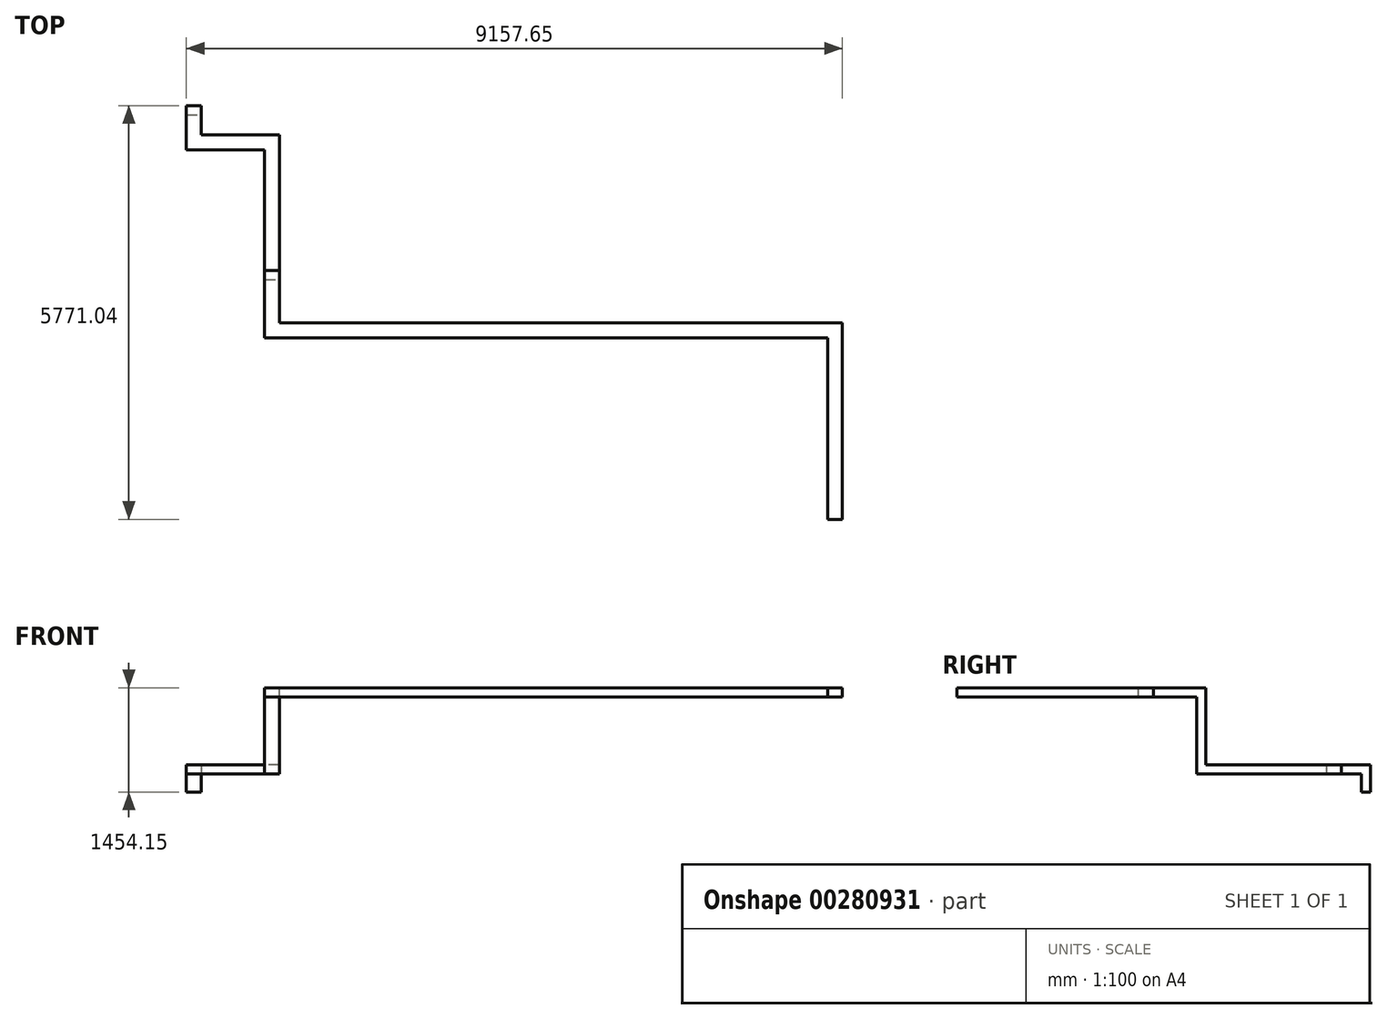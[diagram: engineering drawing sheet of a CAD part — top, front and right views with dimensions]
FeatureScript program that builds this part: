
annotation { "Feature Type Name" : "Feature", "Feature Type Description" : "" }
export const myFeature = defineFeature(function(context is Context, id is Id, definition is map)
    precondition{}
    {
        {
            var Q0;
            Q0=qCreatedBy(makeId("Top.planeOp"),FACE);
            var sketch = newSketch(context, id + "F0", { "sketchPlane" : qUnion([Q0])});
            skLineSegment(sketch, "E0.bottom", {"start": v(0, 0) * mm, "end": v(208.28, 0) * mm});
            skLineSegment(sketch, "E0.top", {"start": v(0, 127) * mm, "end": v(208.28, 127) * mm});
            skLineSegment(sketch, "E0.left", {"start": v(0, 0) * mm, "end": v(0, 127) * mm});
            skLineSegment(sketch, "E0.right", {"start": v(208.28, 0) * mm, "end": v(208.28, 127) * mm});
            skSolve(sketch);
        }
        {
            var Q0;
            Q0=makeQuery(id+"F0.imprint","IMPRINT",FACE,{"disambiguationData":[TD([[makeQuery(id+"F0.imprint","IMPRINT",EDGE,{"derivedFrom":sQuery(id+"F0.wireOp",EDGE,"E0.bottom")}),1.0]])]});
            extrude(context, id + "F1", {"entities" : qUnion([Q0]), "depth" : 381 * mm});
        }
        {
            var Q0;
            Q0=makeQuery(id+"F1.opExtrude","SWEPT_FACE",FACE,{"disambiguationData":[OSD([sQuery(id+"F0.wireOp",EDGE,"E0.bottom")])]});
            var sketch = newSketch(context, id + "F2", { "sketchPlane" : qUnion([Q0])});
            skLineSegment(sketch, "E1.bottom", {"start": v(0, 381) * mm, "end": v(208.28, 381) * mm});
            skLineSegment(sketch, "E1.top", {"start": v(0, 254) * mm, "end": v(208.28, 254) * mm});
            skLineSegment(sketch, "E1.left", {"start": v(0, 381) * mm, "end": v(0, 254) * mm});
            skLineSegment(sketch, "E1.right", {"start": v(208.28, 381) * mm, "end": v(208.28, 254) * mm});
            skSolve(sketch);
        }
        {
            var Q0;
            Q0=makeQuery(id+"F2.imprint","IMPRINT",FACE,{"disambiguationData":[TD([[makeQuery(id+"F2.imprint","IMPRINT",EDGE,{"derivedFrom":sQuery(id+"F2.wireOp",EDGE,"E1.bottom")}),-1.0]])]});
            extrude(context, id + "F3", {"entities" : qUnion([Q0]), "operationType" : NewBodyOperationType.ADD, "depth" : 1524 * mm});
        }
        {
            var Q0;
            Q0=makeQuery(id+"F3.opExtrude","CAP_FACE",FACE,{"disambiguationData":[OSD([sQuery(id+"F2.wireOp",EDGE,"E1.bottom"),sQuery(id+"F2.wireOp",EDGE,"E1.top"),sQuery(id+"F2.wireOp",EDGE,"E1.left"),sQuery(id+"F2.wireOp",EDGE,"E1.right")])],"isStart":false});
            extrude(context, id + "F4", {"entities" : qUnion([Q0]), "operationType" : NewBodyOperationType.ADD, "depth" : 1612.9 * mm});
        }
        {
            var Q0;
            {var subQ0=sQuery(id+"F2.wireOp",EDGE,"E1.bottom");Q0=makeQuery(id+"F4.boolean.opBoolean","MERGE",FACE,{"derivedFrom":[makeQuery(id+"F3.boolean.opBoolean","MERGE",FACE,{"derivedFrom":[makeQuery(id+"F1.opExtrude","CAP_FACE",FACE,{"disambiguationData":[OSD([sQuery(id+"F0.wireOp",EDGE,"E0.bottom"),sQuery(id+"F0.wireOp",EDGE,"E0.top"),sQuery(id+"F0.wireOp",EDGE,"E0.left"),sQuery(id+"F0.wireOp",EDGE,"E0.right")])],"isStart":false}),makeQuery(id+"F3.opExtrude","SWEPT_FACE",FACE,{"disambiguationData":[OSD([subQ0])]})]}),makeQuery(id+"F4.opExtrude","SWEPT_FACE",FACE,{"disambiguationData":[OSD([subQ0])]})]});}
            var sketch = newSketch(context, id + "F5", { "sketchPlane" : qUnion([Q0])});
            skLineSegment(sketch, "E2.bottom", {"start": v(208.28, -3136.9) * mm, "end": v(0, -3136.9) * mm});
            skLineSegment(sketch, "E2.top", {"start": v(208.28, -3009.9) * mm, "end": v(0, -3009.9) * mm});
            skLineSegment(sketch, "E2.left", {"start": v(208.28, -3136.9) * mm, "end": v(208.28, -3009.9) * mm});
            skLineSegment(sketch, "E2.right", {"start": v(0, -3136.9) * mm, "end": v(0, -3009.9) * mm});
            skSolve(sketch);
        }
        {
            var Q0;
            Q0=makeQuery(id+"F5.imprint","IMPRINT",FACE,{"disambiguationData":[TD([[makeQuery(id+"F5.imprint","IMPRINT",EDGE,{"derivedFrom":sQuery(id+"F5.wireOp",EDGE,"E2.bottom")}),1.0]])]});
            extrude(context, id + "F6", {"entities" : qUnion([Q0]), "operationType" : NewBodyOperationType.ADD, "depth" : 863.6 * mm});
        }
        {
            var Q0;
            {var subQ0=sQuery(id+"F2.wireOp",EDGE,"E1.right");Q0=makeQuery(id+"F6.boolean.opBoolean","MERGE",FACE,{"derivedFrom":[makeQuery(id+"F4.boolean.opBoolean","MERGE",FACE,{"derivedFrom":[makeQuery(id+"F3.boolean.opBoolean","MERGE",FACE,{"derivedFrom":[makeQuery(id+"F1.opExtrude","SWEPT_FACE",FACE,{"disambiguationData":[OSD([sQuery(id+"F0.wireOp",EDGE,"E0.right")])]}),makeQuery(id+"F3.opExtrude","SWEPT_FACE",FACE,{"disambiguationData":[OSD([subQ0])]})]}),makeQuery(id+"F4.opExtrude","SWEPT_FACE",FACE,{"disambiguationData":[OSD([subQ0])]})]}),makeQuery(id+"F6.opExtrude","SWEPT_FACE",FACE,{"disambiguationData":[OSD([sQuery(id+"F5.wireOp",EDGE,"E2.left")])]})]});}
            var sketch = newSketch(context, id + "F7", { "sketchPlane" : qUnion([Q0])});
            skLineSegment(sketch, "E3.bottom", {"start": v(-3136.9, 1244.6) * mm, "end": v(-3009.9, 1244.6) * mm});
            skLineSegment(sketch, "E3.top", {"start": v(-3136.9, 1036.32) * mm, "end": v(-3009.9, 1036.32) * mm});
            skLineSegment(sketch, "E3.left", {"start": v(-3136.9, 1244.6) * mm, "end": v(-3136.9, 1036.32) * mm});
            skLineSegment(sketch, "E3.right", {"start": v(-3009.9, 1244.6) * mm, "end": v(-3009.9, 1036.32) * mm});
            skSolve(sketch);
        }
        {
            var Q0;
            Q0=makeQuery(id+"F7.imprint","IMPRINT",FACE,{"disambiguationData":[TD([[makeQuery(id+"F7.imprint","IMPRINT",EDGE,{"derivedFrom":sQuery(id+"F7.wireOp",EDGE,"E3.bottom")}),-1.0]])]});
            extrude(context, id + "F8", {"entities" : qUnion([Q0]), "operationType" : NewBodyOperationType.ADD, "depth" : 7112 * mm});
        }
        {
            var Q0;
            Q0=makeQuery(id+"F8.boolean.opBoolean","MERGE",FACE,{"derivedFrom":[makeQuery(id+"F6.opExtrude","SWEPT_FACE",FACE,{"disambiguationData":[OSD([sQuery(id+"F5.wireOp",EDGE,"E2.top")])]}),makeQuery(id+"F8.opExtrude","SWEPT_FACE",FACE,{"disambiguationData":[OSD([sQuery(id+"F7.wireOp",EDGE,"E3.right")])]})]});
            extrude(context, id + "F9", {"entities" : qUnion([Q0]), "operationType" : NewBodyOperationType.ADD, "depth" : 762 * mm});
        }
        {
            var Q0;
            Q0=makeQuery(id+"F8.boolean.opBoolean","MERGE",FACE,{"derivedFrom":[makeQuery(id+"F6.boolean.opBoolean","MERGE",FACE,{"derivedFrom":[makeQuery(id+"F4.opExtrude","CAP_FACE",FACE,{"disambiguationData":[OSD([sQuery(id+"F2.wireOp",EDGE,"E1.bottom"),sQuery(id+"F2.wireOp",EDGE,"E1.top"),sQuery(id+"F2.wireOp",EDGE,"E1.left"),sQuery(id+"F2.wireOp",EDGE,"E1.right")])],"isStart":false}),makeQuery(id+"F6.opExtrude","SWEPT_FACE",FACE,{"disambiguationData":[OSD([sQuery(id+"F5.wireOp",EDGE,"E2.bottom")])]})]}),makeQuery(id+"F8.opExtrude","SWEPT_FACE",FACE,{"disambiguationData":[OSD([sQuery(id+"F7.wireOp",EDGE,"E3.left")])]})]});
            extrude(context, id + "F10", {"entities" : qUnion([Q0]), "operationType" : NewBodyOperationType.REMOVE, "oppositeDirection" : true, "depth" : 762 * mm});
        }
        {
            var Q0;
            {var subQ0=sQuery(id+"F7.wireOp",EDGE,"E3.right");Q0=makeQuery(id+"F9.boolean.opBoolean","MERGE",FACE,{"derivedFrom":[makeQuery(id+"F8.opExtrude","CAP_FACE",FACE,{"disambiguationData":[OSD([sQuery(id+"F7.wireOp",EDGE,"E3.bottom"),sQuery(id+"F7.wireOp",EDGE,"E3.top"),sQuery(id+"F7.wireOp",EDGE,"E3.left"),subQ0])],"isStart":false}),makeQuery(id+"F9.opExtrude","SWEPT_FACE",FACE,{"disambiguationData":[OSD([subQ0])]})]});}
            var Q1;
            {var subQ0=sQuery(id+"F5.wireOp",EDGE,"E2.left");var subQ1=sQuery(id+"F2.wireOp",EDGE,"E1.right");var subQ2=sQuery(id+"F0.wireOp",EDGE,"E0.right");Q1=makeQuery(id+"F9.boolean.opBoolean","MERGE",FACE,{"derivedFrom":[makeQuery(id+"F6.boolean.opBoolean","MERGE",FACE,{"derivedFrom":[makeQuery(id+"F4.boolean.opBoolean","MERGE",FACE,{"derivedFrom":[makeQuery(id+"F3.boolean.opBoolean","MERGE",FACE,{"derivedFrom":[makeQuery(id+"F1.opExtrude","SWEPT_FACE",FACE,{"disambiguationData":[OSD([subQ2])]}),makeQuery(id+"F3.opExtrude","SWEPT_FACE",FACE,{"disambiguationData":[OSD([subQ1])]})]}),makeQuery(id+"F4.opExtrude","SWEPT_FACE",FACE,{"disambiguationData":[OSD([subQ1])]})]}),makeQuery(id+"F6.opExtrude","SWEPT_FACE",FACE,{"disambiguationData":[OSD([subQ0])]})]}),makeQuery(id+"F9.opExtrude","SWEPT_FACE",FACE,{"disambiguationData":[OSD([subQ2,sQuery(id+"F2.wireOp",EDGE,"E1.bottom"),subQ1,sQuery(id+"F5.wireOp",EDGE,"E2.top"),subQ0])]})]});}
            extrude(context, id + "F11", {"entities" : qUnion([Q0]), "operationType" : NewBodyOperationType.REMOVE, "endBound" : BoundingType.UP_TO_SURFACE, "oppositeDirection" : true, "endBoundEntityFace" : qUnion([Q1]), "depth" : 25.4 * mm});
        }
        {
            var Q0;
            Q0=makeQuery(id+"F10.boolean.opBoolean","COPY",FACE,{"derivedFrom":makeQuery(id+"F10.opExtrude","CAP_FACE",FACE,{"disambiguationData":[OSD([sQuery(id+"F2.wireOp",EDGE,"E1.bottom"),sQuery(id+"F2.wireOp",EDGE,"E1.top"),sQuery(id+"F2.wireOp",EDGE,"E1.left"),sQuery(id+"F2.wireOp",EDGE,"E1.right"),sQuery(id+"F5.wireOp",EDGE,"E2.bottom"),sQuery(id+"F7.wireOp",EDGE,"E3.left")])],"isStart":false})});
            var sketch = newSketch(context, id + "F12", { "sketchPlane" : qUnion([Q0])});
            skLineSegment(sketch, "E4.bottom", {"start": v(0, 1244.6) * mm, "end": v(208.28, 1244.6) * mm});
            skLineSegment(sketch, "E4.top", {"start": v(0, 1117.6) * mm, "end": v(208.28, 1117.6) * mm});
            skLineSegment(sketch, "E4.left", {"start": v(0, 1244.6) * mm, "end": v(0, 1117.6) * mm});
            skLineSegment(sketch, "E4.right", {"start": v(208.28, 1244.6) * mm, "end": v(208.28, 1117.6) * mm});
            skSolve(sketch);
        }
        {
            var Q0;
            Q0=makeQuery(id+"F12.imprint","IMPRINT",FACE,{"disambiguationData":[TD([[makeQuery(id+"F12.imprint","IMPRINT",EDGE,{"derivedFrom":sQuery(id+"F12.wireOp",EDGE,"E4.bottom")}),-1.0]])]});
            extrude(context, id + "F13", {"entities" : qUnion([Q0]), "operationType" : NewBodyOperationType.ADD, "depth" : 762 * mm});
        }
        {
            var Q0;
            {var subQ0=sQuery(id+"F5.wireOp",EDGE,"E2.left");var subQ1=sQuery(id+"F5.wireOp",EDGE,"E2.top");var subQ2=sQuery(id+"F2.wireOp",EDGE,"E1.right");var subQ3=sQuery(id+"F2.wireOp",EDGE,"E1.bottom");var subQ4=sQuery(id+"F0.wireOp",EDGE,"E0.right");Q0=makeQuery(id+"F13.boolean.opBoolean","MERGE",FACE,{"derivedFrom":[makeQuery(id+"F11.boolean.opBoolean","MERGE",FACE,{"derivedFrom":[makeQuery(id+"F9.boolean.opBoolean","MERGE",FACE,{"derivedFrom":[makeQuery(id+"F6.boolean.opBoolean","MERGE",FACE,{"derivedFrom":[makeQuery(id+"F4.boolean.opBoolean","MERGE",FACE,{"derivedFrom":[makeQuery(id+"F3.boolean.opBoolean","MERGE",FACE,{"derivedFrom":[makeQuery(id+"F1.opExtrude","SWEPT_FACE",FACE,{"disambiguationData":[OSD([subQ4])]}),makeQuery(id+"F3.opExtrude","SWEPT_FACE",FACE,{"disambiguationData":[OSD([subQ2])]})]}),makeQuery(id+"F4.opExtrude","SWEPT_FACE",FACE,{"disambiguationData":[OSD([subQ2])]})]}),makeQuery(id+"F6.opExtrude","SWEPT_FACE",FACE,{"disambiguationData":[OSD([subQ0])]})]}),makeQuery(id+"F9.opExtrude","SWEPT_FACE",FACE,{"disambiguationData":[OSD([subQ4,subQ3,subQ2,subQ1,subQ0])]})]}),makeQuery(id+"F11.opExtrude","CAP_FACE",FACE,{"disambiguationData":[OSD([subQ4,subQ3,subQ2,subQ1,subQ0])],"isStart":false})]}),makeQuery(id+"F13.opExtrude","SWEPT_FACE",FACE,{"disambiguationData":[OSD([sQuery(id+"F12.wireOp",EDGE,"E4.right")])]})]});}
            var sketch = newSketch(context, id + "F14", { "sketchPlane" : qUnion([Q0])});
            skLineSegment(sketch, "E5.bottom", {"start": v(-3136.9, 1244.6) * mm, "end": v(-2928.62, 1244.6) * mm});
            skLineSegment(sketch, "E5.top", {"start": v(-3136.9, 1117.6) * mm, "end": v(-2928.62, 1117.6) * mm});
            skLineSegment(sketch, "E5.left", {"start": v(-3136.9, 1244.6) * mm, "end": v(-3136.9, 1117.6) * mm});
            skLineSegment(sketch, "E5.right", {"start": v(-2928.62, 1244.6) * mm, "end": v(-2928.62, 1117.6) * mm});
            skSolve(sketch);
        }
        {
            var Q0;
            Q0=makeQuery(id+"F14.imprint","IMPRINT",FACE,{"disambiguationData":[TD([[makeQuery(id+"F14.imprint","IMPRINT",EDGE,{"derivedFrom":sQuery(id+"F14.wireOp",EDGE,"E5.bottom")}),-1.0]])]});
            extrude(context, id + "F15", {"entities" : qUnion([Q0]), "operationType" : NewBodyOperationType.ADD, "depth" : 5080 * mm});
        }
        {
            var Q0;
            {var subQ0=sQuery(id+"F7.wireOp",EDGE,"E3.bottom");var subQ1=sQuery(id+"F5.wireOp",EDGE,"E2.top");Q0=makeQuery(id+"F15.boolean.opBoolean","MERGE",FACE,{"derivedFrom":[makeQuery(id+"F13.boolean.opBoolean","MERGE",FACE,{"derivedFrom":[makeQuery(id+"F9.boolean.opBoolean","MERGE",FACE,{"derivedFrom":[makeQuery(id+"F8.boolean.opBoolean","MERGE",FACE,{"derivedFrom":[makeQuery(id+"F6.opExtrude","CAP_FACE",FACE,{"disambiguationData":[OSD([sQuery(id+"F5.wireOp",EDGE,"E2.bottom"),subQ1,sQuery(id+"F5.wireOp",EDGE,"E2.left"),sQuery(id+"F5.wireOp",EDGE,"E2.right")])],"isStart":false}),makeQuery(id+"F8.opExtrude","SWEPT_FACE",FACE,{"disambiguationData":[OSD([subQ0])]})]}),makeQuery(id+"F9.opExtrude","SWEPT_FACE",FACE,{"disambiguationData":[OSD([subQ1,subQ0,sQuery(id+"F7.wireOp",EDGE,"E3.right")])]})]}),makeQuery(id+"F13.opExtrude","SWEPT_FACE",FACE,{"disambiguationData":[OSD([sQuery(id+"F12.wireOp",EDGE,"E4.bottom")])]})]}),makeQuery(id+"F15.opExtrude","SWEPT_FACE",FACE,{"disambiguationData":[OSD([sQuery(id+"F14.wireOp",EDGE,"E5.bottom")])]})]});}
            extrude(context, id + "F16", {"entities" : qUnion([Q0]), "operationType" : NewBodyOperationType.ADD, "depth" : 88.9 * mm});
        }
        {
            var Q0;
            Q0=makeQuery(id+"F15.boolean.opBoolean","MERGE",FACE,{"derivedFrom":[makeQuery(id+"F13.opExtrude","SWEPT_FACE",FACE,{"disambiguationData":[OSD([sQuery(id+"F12.wireOp",EDGE,"E4.top")])]}),makeQuery(id+"F15.opExtrude","SWEPT_FACE",FACE,{"disambiguationData":[OSD([sQuery(id+"F14.wireOp",EDGE,"E5.top")])]})]});
            extrude(context, id + "F17", {"entities" : qUnion([Q0]), "operationType" : NewBodyOperationType.REMOVE, "oppositeDirection" : true, "depth" : 88.9 * mm});
        }
        {
            var Q0;
            Q0=makeQuery(id+"F16.opExtrude","CAP_FACE",FACE,{"disambiguationData":[OSD([sQuery(id+"F5.wireOp",EDGE,"E2.bottom"),sQuery(id+"F5.wireOp",EDGE,"E2.top"),sQuery(id+"F5.wireOp",EDGE,"E2.left"),sQuery(id+"F5.wireOp",EDGE,"E2.right"),sQuery(id+"F7.wireOp",EDGE,"E3.bottom"),sQuery(id+"F7.wireOp",EDGE,"E3.right"),sQuery(id+"F12.wireOp",EDGE,"E4.bottom"),sQuery(id+"F14.wireOp",EDGE,"E5.bottom")])],"isStart":false});
            extrude(context, id + "F18", {"entities" : qUnion([Q0]), "operationType" : NewBodyOperationType.ADD, "depth" : 120.65 * mm});
        }
        {
            var Q0;
            Q0=makeQuery(id+"F17.boolean.opBoolean","COPY",FACE,{"derivedFrom":makeQuery(id+"F17.opExtrude","CAP_FACE",FACE,{"disambiguationData":[OSD([sQuery(id+"F12.wireOp",EDGE,"E4.top"),sQuery(id+"F14.wireOp",EDGE,"E5.top")])],"isStart":false})});
            extrude(context, id + "F19", {"entities" : qUnion([Q0]), "operationType" : NewBodyOperationType.REMOVE, "oppositeDirection" : true, "depth" : 120.65 * mm});
        }
        {
            var Q0;
            {var subQ0=sQuery(id+"F14.wireOp",EDGE,"E5.bottom");Q0=makeQuery(id+"F18.boolean.opBoolean","MERGE",FACE,{"derivedFrom":[makeQuery(id+"F16.boolean.opBoolean","MERGE",FACE,{"derivedFrom":[makeQuery(id+"F15.opExtrude","CAP_FACE",FACE,{"disambiguationData":[OSD([subQ0,sQuery(id+"F14.wireOp",EDGE,"E5.top"),sQuery(id+"F14.wireOp",EDGE,"E5.left"),sQuery(id+"F14.wireOp",EDGE,"E5.right")])],"isStart":false}),makeQuery(id+"F16.opExtrude","SWEPT_FACE",FACE,{"disambiguationData":[OSD([subQ0])]})]}),makeQuery(id+"F18.opExtrude","SWEPT_FACE",FACE,{"disambiguationData":[OSD([subQ0])]})]});}
            extrude(context, id + "F20", {"entities" : qUnion([Q0]), "operationType" : NewBodyOperationType.ADD, "depth" : 2312.35 * mm});
        }
        {
            var Q0;
            {var subQ0=sQuery(id+"F14.wireOp",EDGE,"E5.left");var subQ1=sQuery(id+"F14.wireOp",EDGE,"E5.bottom");var subQ2=sQuery(id+"F12.wireOp",EDGE,"E4.bottom");Q0=makeQuery(id+"F20.boolean.opBoolean","MERGE",FACE,{"derivedFrom":[makeQuery(id+"F18.boolean.opBoolean","MERGE",FACE,{"derivedFrom":[makeQuery(id+"F16.boolean.opBoolean","MERGE",FACE,{"derivedFrom":[makeQuery(id+"F15.boolean.opBoolean","MERGE",FACE,{"derivedFrom":[makeQuery(id+"F13.opExtrude","CAP_FACE",FACE,{"disambiguationData":[OSD([subQ2,sQuery(id+"F12.wireOp",EDGE,"E4.top"),sQuery(id+"F12.wireOp",EDGE,"E4.left"),sQuery(id+"F12.wireOp",EDGE,"E4.right")])],"isStart":false}),makeQuery(id+"F15.opExtrude","SWEPT_FACE",FACE,{"disambiguationData":[OSD([subQ0])]})]}),makeQuery(id+"F16.opExtrude","SWEPT_FACE",FACE,{"disambiguationData":[OSD([subQ2,subQ1,subQ0])]})]}),makeQuery(id+"F18.opExtrude","SWEPT_FACE",FACE,{"disambiguationData":[OSD([subQ2,subQ1,subQ0])]})]}),makeQuery(id+"F20.opExtrude","SWEPT_FACE",FACE,{"disambiguationData":[OSD([subQ1,subQ0])]})]});}
            var sketch = newSketch(context, id + "F21", { "sketchPlane" : qUnion([Q0])});
            skLineSegment(sketch, "E6.bottom", {"start": v(7600.63, 1327.15) * mm, "end": v(7392.35, 1327.15) * mm});
            skLineSegment(sketch, "E6.top", {"start": v(7600.63, 1454.15) * mm, "end": v(7392.35, 1454.15) * mm});
            skLineSegment(sketch, "E6.left", {"start": v(7600.63, 1327.15) * mm, "end": v(7600.63, 1454.15) * mm});
            skLineSegment(sketch, "E6.right", {"start": v(7392.35, 1327.15) * mm, "end": v(7392.35, 1454.15) * mm});
            skSolve(sketch);
        }
        {
            var Q0;
            Q0=makeQuery(id+"F21.imprint","IMPRINT",FACE,{"disambiguationData":[TD([[makeQuery(id+"F21.imprint","IMPRINT",EDGE,{"derivedFrom":sQuery(id+"F21.wireOp",EDGE,"E6.bottom")}),1.0]])]});
            extrude(context, id + "F22", {"entities" : qUnion([Q0]), "operationType" : NewBodyOperationType.ADD, "depth" : 2583.34 * mm});
        }
        {
            var Q0;
            {var subQ0=sQuery(id+"F12.wireOp",EDGE,"E4.left");var subQ1=sQuery(id+"F12.wireOp",EDGE,"E4.bottom");var subQ2=sQuery(id+"F5.wireOp",EDGE,"E2.right");var subQ3=sQuery(id+"F5.wireOp",EDGE,"E2.top");var subQ4=sQuery(id+"F2.wireOp",EDGE,"E1.left");var subQ5=sQuery(id+"F2.wireOp",EDGE,"E1.bottom");var subQ6=sQuery(id+"F0.wireOp",EDGE,"E0.left");Q0=makeQuery(id+"F18.boolean.opBoolean","MERGE",FACE,{"derivedFrom":[makeQuery(id+"F16.boolean.opBoolean","MERGE",FACE,{"derivedFrom":[makeQuery(id+"F13.boolean.opBoolean","MERGE",FACE,{"derivedFrom":[makeQuery(id+"F9.boolean.opBoolean","MERGE",FACE,{"derivedFrom":[makeQuery(id+"F6.boolean.opBoolean","MERGE",FACE,{"derivedFrom":[makeQuery(id+"F4.boolean.opBoolean","MERGE",FACE,{"derivedFrom":[makeQuery(id+"F3.boolean.opBoolean","MERGE",FACE,{"derivedFrom":[makeQuery(id+"F1.opExtrude","SWEPT_FACE",FACE,{"disambiguationData":[OSD([subQ6])]}),makeQuery(id+"F3.opExtrude","SWEPT_FACE",FACE,{"disambiguationData":[OSD([subQ4])]})]}),makeQuery(id+"F4.opExtrude","SWEPT_FACE",FACE,{"disambiguationData":[OSD([subQ4])]})]}),makeQuery(id+"F6.opExtrude","SWEPT_FACE",FACE,{"disambiguationData":[OSD([subQ2])]})]}),makeQuery(id+"F9.opExtrude","SWEPT_FACE",FACE,{"disambiguationData":[OSD([subQ6,subQ5,subQ4,subQ3,subQ2])]})]}),makeQuery(id+"F13.opExtrude","SWEPT_FACE",FACE,{"disambiguationData":[OSD([subQ0])]})]}),makeQuery(id+"F16.opExtrude","SWEPT_FACE",FACE,{"disambiguationData":[OSD([subQ6,subQ5,subQ4,subQ3,subQ2,subQ1,subQ0])]})]}),makeQuery(id+"F18.opExtrude","SWEPT_FACE",FACE,{"disambiguationData":[OSD([subQ6,subQ5,subQ4,subQ3,subQ2,subQ1,subQ0])]})]});}
            extrude(context, id + "F23", {"entities" : qUnion([Q0]), "operationType" : NewBodyOperationType.ADD, "depth" : 1557.02 * mm});
        }
        {
            var Q0;
            {var subQ0=sQuery(id+"F12.wireOp",EDGE,"E4.right");var subQ1=sQuery(id+"F12.wireOp",EDGE,"E4.bottom");var subQ2=sQuery(id+"F7.wireOp",EDGE,"E3.right");var subQ3=sQuery(id+"F7.wireOp",EDGE,"E3.bottom");var subQ4=sQuery(id+"F5.wireOp",EDGE,"E2.left");var subQ5=sQuery(id+"F5.wireOp",EDGE,"E2.top");var subQ6=sQuery(id+"F2.wireOp",EDGE,"E1.right");var subQ7=sQuery(id+"F2.wireOp",EDGE,"E1.bottom");var subQ8=sQuery(id+"F0.wireOp",EDGE,"E0.right");Q0=makeQuery(id+"F18.boolean.opBoolean","MERGE",FACE,{"derivedFrom":[makeQuery(id+"F16.boolean.opBoolean","MERGE",FACE,{"derivedFrom":[makeQuery(id+"F13.boolean.opBoolean","MERGE",FACE,{"derivedFrom":[makeQuery(id+"F11.boolean.opBoolean","MERGE",FACE,{"derivedFrom":[makeQuery(id+"F9.boolean.opBoolean","MERGE",FACE,{"derivedFrom":[makeQuery(id+"F6.boolean.opBoolean","MERGE",FACE,{"derivedFrom":[makeQuery(id+"F4.boolean.opBoolean","MERGE",FACE,{"derivedFrom":[makeQuery(id+"F3.boolean.opBoolean","MERGE",FACE,{"derivedFrom":[makeQuery(id+"F1.opExtrude","SWEPT_FACE",FACE,{"disambiguationData":[OSD([subQ8])]}),makeQuery(id+"F3.opExtrude","SWEPT_FACE",FACE,{"disambiguationData":[OSD([subQ6])]})]}),makeQuery(id+"F4.opExtrude","SWEPT_FACE",FACE,{"disambiguationData":[OSD([subQ6])]})]}),makeQuery(id+"F6.opExtrude","SWEPT_FACE",FACE,{"disambiguationData":[OSD([subQ4])]})]}),makeQuery(id+"F9.opExtrude","SWEPT_FACE",FACE,{"disambiguationData":[OSD([subQ8,subQ7,subQ6,subQ5,subQ4])]})]}),makeQuery(id+"F11.opExtrude","CAP_FACE",FACE,{"disambiguationData":[OSD([subQ8,subQ7,subQ6,subQ5,subQ4])],"isStart":false})]}),makeQuery(id+"F13.opExtrude","SWEPT_FACE",FACE,{"disambiguationData":[OSD([subQ0])]})]}),makeQuery(id+"F16.opExtrude","SWEPT_FACE",FACE,{"disambiguationData":[OSD([subQ8,subQ7,subQ6,subQ5,subQ4,subQ3,subQ2,subQ1,subQ0])]})]}),makeQuery(id+"F18.opExtrude","SWEPT_FACE",FACE,{"disambiguationData":[OSD([subQ8,subQ7,subQ6,subQ5,subQ4,subQ3,subQ2,subQ1,subQ0])]})]});}
            extrude(context, id + "F24", {"entities" : qUnion([Q0]), "operationType" : NewBodyOperationType.REMOVE, "oppositeDirection" : true, "depth" : 1557.02 * mm});
        }
        {
            var Q0;
            Q0=makeQuery(id+"F24.boolean.opBoolean","COPY",FACE,{"derivedFrom":makeQuery(id+"F24.opExtrude","CAP_FACE",FACE,{"disambiguationData":[OSD([sQuery(id+"F0.wireOp",EDGE,"E0.right"),sQuery(id+"F2.wireOp",EDGE,"E1.bottom"),sQuery(id+"F2.wireOp",EDGE,"E1.right"),sQuery(id+"F5.wireOp",EDGE,"E2.top"),sQuery(id+"F5.wireOp",EDGE,"E2.left"),sQuery(id+"F7.wireOp",EDGE,"E3.bottom"),sQuery(id+"F7.wireOp",EDGE,"E3.right"),sQuery(id+"F12.wireOp",EDGE,"E4.bottom"),sQuery(id+"F12.wireOp",EDGE,"E4.right")])],"isStart":false})});
            var sketch = newSketch(context, id + "F25", { "sketchPlane" : qUnion([Q0])});
            skLineSegment(sketch, "E7.bottom", {"start": v(0, 254) * mm, "end": v(-355.6, 254) * mm, "construction": true});
            skLineSegment(sketch, "E7.top", {"start": v(0, 381) * mm, "end": v(-355.6, 381) * mm, "construction": true});
            skLineSegment(sketch, "E7.left", {"start": v(0, 254) * mm, "end": v(0, 381) * mm, "construction": true});
            skLineSegment(sketch, "E7.right", {"start": v(-355.6, 254) * mm, "end": v(-355.6, 381) * mm, "construction": true});
            skLineSegment(sketch, "E8.bottom", {"start": v(-355.6, 381) * mm, "end": v(-563.88, 381) * mm});
            skLineSegment(sketch, "E8.top", {"start": v(-355.6, 254) * mm, "end": v(-563.88, 254) * mm});
            skLineSegment(sketch, "E8.left", {"start": v(-355.6, 381) * mm, "end": v(-355.6, 254) * mm});
            skLineSegment(sketch, "E8.right", {"start": v(-563.88, 381) * mm, "end": v(-563.88, 254) * mm});
            skSolve(sketch);
        }
        {
            var Q0;
            Q0=makeQuery(id+"F25.imprint","IMPRINT",FACE,{"disambiguationData":[TD([[makeQuery(id+"F25.imprint","IMPRINT",EDGE,{"derivedFrom":sQuery(id+"F25.wireOp",EDGE,"E8.bottom")}),-1.0]])]});
            extrude(context, id + "F26", {"entities" : qUnion([Q0]), "operationType" : NewBodyOperationType.ADD, "depth" : 1092.2 * mm});
        }
        {
            var Q0;
            Q0=makeQuery(id+"F26.opExtrude","SWEPT_FACE",FACE,{"disambiguationData":[OSD([sQuery(id+"F25.wireOp",EDGE,"E8.right")])]});
            var sketch = newSketch(context, id + "F27", { "sketchPlane" : qUnion([Q0])});
            skLineSegment(sketch, "E9.bottom", {"start": v(-256.54, 254) * mm, "end": v(-464.82, 254) * mm});
            skLineSegment(sketch, "E9.top", {"start": v(-256.54, 381) * mm, "end": v(-464.82, 381) * mm});
            skLineSegment(sketch, "E9.left", {"start": v(-256.54, 254) * mm, "end": v(-256.54, 381) * mm});
            skLineSegment(sketch, "E9.right", {"start": v(-464.82, 254) * mm, "end": v(-464.82, 381) * mm});
            skSolve(sketch);
        }
        {
            var Q0;
            Q0=makeQuery(id+"F27.imprint","IMPRINT",FACE,{"disambiguationData":[TD([[makeQuery(id+"F27.imprint","IMPRINT",EDGE,{"derivedFrom":sQuery(id+"F27.wireOp",EDGE,"E9.bottom")}),-1.0]])]});
            var Q1;
            {var subQ0=sQuery(id+"F12.wireOp",EDGE,"E4.left");var subQ1=sQuery(id+"F12.wireOp",EDGE,"E4.top");var subQ2=sQuery(id+"F5.wireOp",EDGE,"E2.right");var subQ3=sQuery(id+"F5.wireOp",EDGE,"E2.bottom");var subQ4=sQuery(id+"F2.wireOp",EDGE,"E1.left");var subQ5=makeQuery(id+"F13.opExtrude","CAP_VERTEX",VERTEX,{"disambiguationData":[OSD([subQ4,subQ3,subQ2,subQ1,subQ0])],"isStart":true});Q1=makeQuery(id+"F23.boolean.opBoolean","MERGE",FACE,{"derivedFrom":[makeQuery(id+"F19.boolean.opBoolean","MERGE",FACE,{"derivedFrom":[makeQuery(id+"F17.boolean.opBoolean","MERGE",FACE,{"derivedFrom":[makeQuery(id+"F10.boolean.opBoolean","COPY",FACE,{"derivedFrom":makeQuery(id+"F10.opExtrude","CAP_FACE",FACE,{"disambiguationData":[OSD([sQuery(id+"F2.wireOp",EDGE,"E1.bottom"),sQuery(id+"F2.wireOp",EDGE,"E1.top"),subQ4,sQuery(id+"F2.wireOp",EDGE,"E1.right"),subQ3,sQuery(id+"F7.wireOp",EDGE,"E3.left")])],"isStart":false})}),makeQuery(id+"F17.opExtrude","SWEPT_FACE",FACE,{"disambiguationData":[OSD([subQ1])]})]}),makeQuery(id+"F19.opExtrude","SWEPT_FACE",FACE,{"disambiguationData":[OSD([subQ1])]})]}),makeQuery(id+"F23.opExtrude","SWEPT_FACE",FACE,{"disambiguationData":[OSD([subQ4,subQ3,subQ2,subQ1,subQ0]),TDD([makeQuery(id+"F19.boolean.opBoolean","MERGE",EDGE,{"derivedFrom":[makeQuery(id+"F17.boolean.opBoolean","MERGE",EDGE,{"derivedFrom":[makeQuery(id+"F10.boolean.opBoolean","COPY",EDGE,{"derivedFrom":makeQuery(id+"F10.opExtrude","CAP_EDGE",EDGE,{"disambiguationData":[OSD([subQ4,subQ3,subQ2])],"isStart":false})}),makeQuery(id+"F17.opExtrude","SWEPT_EDGE",EDGE,{"disambiguationData":[OSD([subQ4,subQ3,subQ2,subQ1,subQ0]),TDD([subQ5])]})]}),makeQuery(id+"F19.opExtrude","SWEPT_EDGE",EDGE,{"disambiguationData":[OSD([subQ4,subQ3,subQ2,subQ1,subQ0]),TDD([makeQuery(id+"F17.boolean.opBoolean","COPY",VERTEX,{"derivedFrom":makeQuery(id+"F17.opExtrude","CAP_VERTEX",VERTEX,{"disambiguationData":[OSD([subQ4,subQ3,subQ2,subQ1,subQ0]),TDD([subQ5])],"isStart":false})})])]})]})])]})]});}
            extrude(context, id + "F28", {"entities" : qUnion([Q0]), "operationType" : NewBodyOperationType.ADD, "endBound" : BoundingType.UP_TO_SURFACE, "endBoundEntityFace" : qUnion([Q1]), "depth" : 25.4 * mm});
        }
        {
            var Q0;
            {var subQ0=sQuery(id+"F2.wireOp",EDGE,"E1.bottom");var subQ1=sQuery(id+"F0.wireOp",EDGE,"E0.left");Q0=makeQuery(id+"F28.boolean.opBoolean","MERGE",FACE,{"derivedFrom":[makeQuery(id+"F26.boolean.opBoolean","MERGE",FACE,{"derivedFrom":[makeQuery(id+"F23.boolean.opBoolean","MERGE",FACE,{"derivedFrom":[makeQuery(id+"F4.boolean.opBoolean","MERGE",FACE,{"derivedFrom":[makeQuery(id+"F3.boolean.opBoolean","MERGE",FACE,{"derivedFrom":[makeQuery(id+"F1.opExtrude","CAP_FACE",FACE,{"disambiguationData":[OSD([sQuery(id+"F0.wireOp",EDGE,"E0.bottom"),sQuery(id+"F0.wireOp",EDGE,"E0.top"),subQ1,sQuery(id+"F0.wireOp",EDGE,"E0.right")])],"isStart":false}),makeQuery(id+"F3.opExtrude","SWEPT_FACE",FACE,{"disambiguationData":[OSD([subQ0])]})]}),makeQuery(id+"F4.opExtrude","SWEPT_FACE",FACE,{"disambiguationData":[OSD([subQ0])]})]}),makeQuery(id+"F23.opExtrude","SWEPT_FACE",FACE,{"disambiguationData":[OSD([subQ1,subQ0,sQuery(id+"F2.wireOp",EDGE,"E1.left")])]})]}),makeQuery(id+"F26.opExtrude","SWEPT_FACE",FACE,{"disambiguationData":[OSD([sQuery(id+"F25.wireOp",EDGE,"E8.bottom")])]})]}),makeQuery(id+"F28.opExtrude","SWEPT_FACE",FACE,{"disambiguationData":[OSD([sQuery(id+"F27.wireOp",EDGE,"E9.top")])]})]});}
            var sketch = newSketch(context, id + "F29", { "sketchPlane" : qUnion([Q0])});
            skLineSegment(sketch, "E10.bottom", {"start": v(-256.54, -2374.9) * mm, "end": v(-464.82, -2374.9) * mm});
            skLineSegment(sketch, "E10.top", {"start": v(-256.54, -2247.9) * mm, "end": v(-464.82, -2247.9) * mm});
            skLineSegment(sketch, "E10.left", {"start": v(-256.54, -2374.9) * mm, "end": v(-256.54, -2247.9) * mm});
            skLineSegment(sketch, "E10.right", {"start": v(-464.82, -2374.9) * mm, "end": v(-464.82, -2247.9) * mm});
            skSolve(sketch);
        }
        {
            var Q0;
            Q0=makeQuery(id+"F29.imprint","IMPRINT",FACE,{"disambiguationData":[TD([[makeQuery(id+"F29.imprint","IMPRINT",EDGE,{"derivedFrom":sQuery(id+"F29.wireOp",EDGE,"E10.bottom")}),-1.0]])]});
            var Q1;
            {var subQ0=sQuery(id+"F12.wireOp",EDGE,"E4.bottom");var subQ1=sQuery(id+"F5.wireOp",EDGE,"E2.right");var subQ2=sQuery(id+"F5.wireOp",EDGE,"E2.top");var subQ3=sQuery(id+"F14.wireOp",EDGE,"E5.bottom");Q1=makeQuery(id+"F23.boolean.opBoolean","MERGE",FACE,{"derivedFrom":[makeQuery(id+"F22.boolean.opBoolean","MERGE",FACE,{"derivedFrom":[makeQuery(id+"F20.boolean.opBoolean","MERGE",FACE,{"derivedFrom":[makeQuery(id+"F18.opExtrude","CAP_FACE",FACE,{"disambiguationData":[OSD([sQuery(id+"F5.wireOp",EDGE,"E2.bottom"),subQ2,sQuery(id+"F5.wireOp",EDGE,"E2.left"),subQ1,sQuery(id+"F7.wireOp",EDGE,"E3.bottom"),sQuery(id+"F7.wireOp",EDGE,"E3.right"),subQ0,subQ3])],"isStart":false}),makeQuery(id+"F20.opExtrude","SWEPT_FACE",FACE,{"disambiguationData":[OSD([subQ3])]})]}),makeQuery(id+"F22.opExtrude","SWEPT_FACE",FACE,{"disambiguationData":[OSD([sQuery(id+"F21.wireOp",EDGE,"E6.top")])]})]}),makeQuery(id+"F23.opExtrude","SWEPT_FACE",FACE,{"disambiguationData":[OSD([sQuery(id+"F0.wireOp",EDGE,"E0.left"),sQuery(id+"F2.wireOp",EDGE,"E1.bottom"),sQuery(id+"F2.wireOp",EDGE,"E1.left"),subQ2,subQ1,subQ0,sQuery(id+"F12.wireOp",EDGE,"E4.left")])]})]});}
            extrude(context, id + "F30", {"entities" : qUnion([Q0]), "operationType" : NewBodyOperationType.ADD, "endBound" : BoundingType.UP_TO_SURFACE, "endBoundEntityFace" : qUnion([Q1]), "depth" : 25.4 * mm});
        }
        {
            var Q0;
            Q0=makeQuery(id+"F30.boolean.opBoolean","MERGE",FACE,{"derivedFrom":[makeQuery(id+"F28.opExtrude","CAP_FACE",FACE,{"disambiguationData":[OSD([sQuery(id+"F2.wireOp",EDGE,"E1.bottom"),sQuery(id+"F2.wireOp",EDGE,"E1.top"),sQuery(id+"F2.wireOp",EDGE,"E1.left"),sQuery(id+"F2.wireOp",EDGE,"E1.right"),sQuery(id+"F5.wireOp",EDGE,"E2.bottom"),sQuery(id+"F5.wireOp",EDGE,"E2.right"),sQuery(id+"F7.wireOp",EDGE,"E3.left"),sQuery(id+"F12.wireOp",EDGE,"E4.top"),sQuery(id+"F12.wireOp",EDGE,"E4.left")])],"isStart":false}),makeQuery(id+"F30.opExtrude","SWEPT_FACE",FACE,{"disambiguationData":[OSD([sQuery(id+"F29.wireOp",EDGE,"E10.bottom")])]})]});
            var sketch = newSketch(context, id + "F31", { "sketchPlane" : qUnion([Q0])});
            skLineSegment(sketch, "E11.bottom", {"start": v(-464.82, 1454.15) * mm, "end": v(-256.54, 1454.15) * mm});
            skLineSegment(sketch, "E11.top", {"start": v(-464.82, 1327.15) * mm, "end": v(-256.54, 1327.15) * mm});
            skLineSegment(sketch, "E11.left", {"start": v(-464.82, 1454.15) * mm, "end": v(-464.82, 1327.15) * mm});
            skLineSegment(sketch, "E11.right", {"start": v(-256.54, 1454.15) * mm, "end": v(-256.54, 1327.15) * mm});
            skSolve(sketch);
        }
        {
            var Q0;
            Q0=makeQuery(id+"F31.imprint","IMPRINT",FACE,{"disambiguationData":[TD([[makeQuery(id+"F31.imprint","IMPRINT",EDGE,{"derivedFrom":sQuery(id+"F31.wireOp",EDGE,"E11.bottom")}),1.0]])]});
            var Q1;
            {var subQ0=sQuery(id+"F14.wireOp",EDGE,"E5.right");var subQ1=sQuery(id+"F14.wireOp",EDGE,"E5.bottom");var subQ2=sQuery(id+"F12.wireOp",EDGE,"E4.right");var subQ3=sQuery(id+"F12.wireOp",EDGE,"E4.bottom");var subQ4=sQuery(id+"F7.wireOp",EDGE,"E3.right");var subQ5=sQuery(id+"F7.wireOp",EDGE,"E3.bottom");var subQ6=sQuery(id+"F5.wireOp",EDGE,"E2.left");var subQ7=sQuery(id+"F5.wireOp",EDGE,"E2.top");var subQ8=sQuery(id+"F2.wireOp",EDGE,"E1.right");var subQ9=sQuery(id+"F2.wireOp",EDGE,"E1.bottom");var subQ10=sQuery(id+"F0.wireOp",EDGE,"E0.right");Q1=makeQuery(id+"F24.boolean.opBoolean","MERGE",FACE,{"derivedFrom":[makeQuery(id+"F20.boolean.opBoolean","MERGE",FACE,{"derivedFrom":[makeQuery(id+"F18.boolean.opBoolean","MERGE",FACE,{"derivedFrom":[makeQuery(id+"F16.boolean.opBoolean","MERGE",FACE,{"derivedFrom":[makeQuery(id+"F15.opExtrude","SWEPT_FACE",FACE,{"disambiguationData":[OSD([subQ0])]}),makeQuery(id+"F16.opExtrude","SWEPT_FACE",FACE,{"disambiguationData":[OSD([subQ10,subQ9,subQ8,subQ7,subQ6,subQ5,subQ4,subQ3,subQ2,subQ1,subQ0])]})]}),makeQuery(id+"F18.opExtrude","SWEPT_FACE",FACE,{"disambiguationData":[OSD([subQ10,subQ9,subQ8,subQ7,subQ6,subQ5,subQ4,subQ3,subQ2,subQ1,subQ0])]})]}),makeQuery(id+"F20.opExtrude","SWEPT_FACE",FACE,{"disambiguationData":[OSD([subQ10,subQ9,subQ8,subQ7,subQ6,subQ5,subQ4,subQ3,subQ2,subQ1,subQ0])]})]}),makeQuery(id+"F24.opExtrude","SWEPT_FACE",FACE,{"disambiguationData":[OSD([subQ10,subQ9,subQ8,subQ7,subQ6,subQ5,subQ4,subQ3,subQ2,subQ1,subQ0])]})]});}
            extrude(context, id + "F32", {"entities" : qUnion([Q0]), "operationType" : NewBodyOperationType.ADD, "endBound" : BoundingType.UP_TO_SURFACE, "endBoundEntityFace" : qUnion([Q1]), "depth" : 25.4 * mm});
        }
        {
            var Q0;
            {var subQ0=sQuery(id+"F12.wireOp",EDGE,"E4.left");var subQ1=sQuery(id+"F12.wireOp",EDGE,"E4.top");var subQ2=sQuery(id+"F5.wireOp",EDGE,"E2.right");var subQ3=sQuery(id+"F5.wireOp",EDGE,"E2.bottom");var subQ4=sQuery(id+"F2.wireOp",EDGE,"E1.left");var subQ5=makeQuery(id+"F13.opExtrude","CAP_VERTEX",VERTEX,{"disambiguationData":[OSD([subQ4,subQ3,subQ2,subQ1,subQ0])],"isStart":true});Q0=makeQuery(id+"F23.boolean.opBoolean","MERGE",FACE,{"derivedFrom":[makeQuery(id+"F19.boolean.opBoolean","MERGE",FACE,{"derivedFrom":[makeQuery(id+"F17.boolean.opBoolean","MERGE",FACE,{"derivedFrom":[makeQuery(id+"F10.boolean.opBoolean","COPY",FACE,{"derivedFrom":makeQuery(id+"F10.opExtrude","CAP_FACE",FACE,{"disambiguationData":[OSD([sQuery(id+"F2.wireOp",EDGE,"E1.bottom"),sQuery(id+"F2.wireOp",EDGE,"E1.top"),subQ4,sQuery(id+"F2.wireOp",EDGE,"E1.right"),subQ3,sQuery(id+"F7.wireOp",EDGE,"E3.left")])],"isStart":false})}),makeQuery(id+"F17.opExtrude","SWEPT_FACE",FACE,{"disambiguationData":[OSD([subQ1])]})]}),makeQuery(id+"F19.opExtrude","SWEPT_FACE",FACE,{"disambiguationData":[OSD([subQ1])]})]}),makeQuery(id+"F23.opExtrude","SWEPT_FACE",FACE,{"disambiguationData":[OSD([subQ4,subQ3,subQ2,subQ1,subQ0]),TDD([makeQuery(id+"F19.boolean.opBoolean","MERGE",EDGE,{"derivedFrom":[makeQuery(id+"F17.boolean.opBoolean","MERGE",EDGE,{"derivedFrom":[makeQuery(id+"F10.boolean.opBoolean","COPY",EDGE,{"derivedFrom":makeQuery(id+"F10.opExtrude","CAP_EDGE",EDGE,{"disambiguationData":[OSD([subQ4,subQ3,subQ2])],"isStart":false})}),makeQuery(id+"F17.opExtrude","SWEPT_EDGE",EDGE,{"disambiguationData":[OSD([subQ4,subQ3,subQ2,subQ1,subQ0]),TDD([subQ5])]})]}),makeQuery(id+"F19.opExtrude","SWEPT_EDGE",EDGE,{"disambiguationData":[OSD([subQ4,subQ3,subQ2,subQ1,subQ0]),TDD([makeQuery(id+"F17.boolean.opBoolean","COPY",VERTEX,{"derivedFrom":makeQuery(id+"F17.opExtrude","CAP_VERTEX",VERTEX,{"disambiguationData":[OSD([subQ4,subQ3,subQ2,subQ1,subQ0]),TDD([subQ5])],"isStart":false})})])]})]})])]})]});}
            var sketch = newSketch(context, id + "F33", { "sketchPlane" : qUnion([Q0])});
            skLineSegment(sketch, "E12.bottom", {"start": v(-1348.74, 254) * mm, "end": v(-1557.02, 254) * mm});
            skLineSegment(sketch, "E12.top", {"start": v(-1348.74, 381) * mm, "end": v(-1557.02, 381) * mm});
            skLineSegment(sketch, "E12.left", {"start": v(-1348.74, 254) * mm, "end": v(-1348.74, 381) * mm});
            skLineSegment(sketch, "E12.right", {"start": v(-1557.02, 254) * mm, "end": v(-1557.02, 381) * mm});
            skSolve(sketch);
        }
        {
            var Q0;
            Q0=makeQuery(id+"F33.imprint","IMPRINT",FACE,{"disambiguationData":[TD([[makeQuery(id+"F33.imprint","IMPRINT",EDGE,{"derivedFrom":sQuery(id+"F33.wireOp",EDGE,"E12.bottom")}),1.0]])]});
            var Q1;
            Q1=makeQuery(id+"F26.opExtrude","SWEPT_FACE",FACE,{"disambiguationData":[OSD([sQuery(id+"F25.wireOp",EDGE,"E8.right")])]});
            extrude(context, id + "F34", {"entities" : qUnion([Q0]), "operationType" : NewBodyOperationType.REMOVE, "endBound" : BoundingType.UP_TO_SURFACE, "oppositeDirection" : true, "endBoundEntityFace" : qUnion([Q1]), "depth" : 25.4 * mm});
        }
        {
            var Q0;
            Q0=makeQuery(id+"F34.boolean.opBoolean","COPY",FACE,{"derivedFrom":makeQuery(id+"F34.opExtrude","SWEPT_FACE",FACE,{"disambiguationData":[OSD([sQuery(id+"F33.wireOp",EDGE,"E12.top")])]})});
            var Q1;
            {var subQ0=sQuery(id+"F12.wireOp",EDGE,"E4.left");var subQ1=sQuery(id+"F12.wireOp",EDGE,"E4.top");var subQ2=sQuery(id+"F5.wireOp",EDGE,"E2.right");var subQ3=sQuery(id+"F5.wireOp",EDGE,"E2.bottom");var subQ4=sQuery(id+"F2.wireOp",EDGE,"E1.left");var subQ5=sQuery(id+"F14.wireOp",EDGE,"E5.top");Q1=makeQuery(id+"F32.boolean.opBoolean","MERGE",FACE,{"derivedFrom":[makeQuery(id+"F23.boolean.opBoolean","MERGE",FACE,{"derivedFrom":[makeQuery(id+"F22.boolean.opBoolean","MERGE",FACE,{"derivedFrom":[makeQuery(id+"F20.boolean.opBoolean","MERGE",FACE,{"derivedFrom":[makeQuery(id+"F19.boolean.opBoolean","COPY",FACE,{"derivedFrom":makeQuery(id+"F19.opExtrude","CAP_FACE",FACE,{"disambiguationData":[OSD([subQ1,subQ5])],"isStart":false})}),makeQuery(id+"F20.opExtrude","SWEPT_FACE",FACE,{"disambiguationData":[OSD([subQ5])]})]}),makeQuery(id+"F22.opExtrude","SWEPT_FACE",FACE,{"disambiguationData":[OSD([sQuery(id+"F21.wireOp",EDGE,"E6.bottom")])]})]}),makeQuery(id+"F23.opExtrude","SWEPT_FACE",FACE,{"disambiguationData":[OSD([subQ4,subQ3,subQ2,subQ1,subQ0]),TDD([makeQuery(id+"F19.boolean.opBoolean","COPY",EDGE,{"derivedFrom":makeQuery(id+"F19.opExtrude","CAP_EDGE",EDGE,{"disambiguationData":[OSD([subQ4,subQ3,subQ2,subQ1,subQ0])],"isStart":false})})])]})]}),makeQuery(id+"F32.opExtrude","SWEPT_FACE",FACE,{"disambiguationData":[OSD([sQuery(id+"F31.wireOp",EDGE,"E11.top")])]})]});}
            extrude(context, id + "F35", {"entities" : qUnion([Q0]), "operationType" : NewBodyOperationType.REMOVE, "endBound" : BoundingType.UP_TO_SURFACE, "oppositeDirection" : true, "endBoundEntityFace" : qUnion([Q1]), "depth" : 25.4 * mm});
        }
        {
            var Q0;
            {var subQ0=sQuery(id+"F5.wireOp",EDGE,"E2.top");var subQ1=sQuery(id+"F7.wireOp",EDGE,"E3.right");var subQ2=sQuery(id+"F7.wireOp",EDGE,"E3.bottom");Q0=makeQuery(id+"F23.boolean.opBoolean","MERGE",FACE,{"derivedFrom":[makeQuery(id+"F18.boolean.opBoolean","MERGE",FACE,{"derivedFrom":[makeQuery(id+"F16.boolean.opBoolean","MERGE",FACE,{"derivedFrom":[makeQuery(id+"F9.opExtrude","CAP_FACE",FACE,{"disambiguationData":[OSD([subQ0,subQ1])],"isStart":false}),makeQuery(id+"F16.opExtrude","SWEPT_FACE",FACE,{"disambiguationData":[OSD([subQ0,subQ2,subQ1])]})]}),makeQuery(id+"F18.opExtrude","SWEPT_FACE",FACE,{"disambiguationData":[OSD([subQ0,subQ2,subQ1])]})]}),makeQuery(id+"F23.opExtrude","SWEPT_FACE",FACE,{"disambiguationData":[OSD([sQuery(id+"F0.wireOp",EDGE,"E0.left"),sQuery(id+"F2.wireOp",EDGE,"E1.bottom"),sQuery(id+"F2.wireOp",EDGE,"E1.left"),subQ0,sQuery(id+"F5.wireOp",EDGE,"E2.right")])]})]});}
            var Q1;
            {var subQ0=sQuery(id+"F12.wireOp",EDGE,"E4.right");var subQ1=sQuery(id+"F12.wireOp",EDGE,"E4.bottom");var subQ2=sQuery(id+"F7.wireOp",EDGE,"E3.right");var subQ3=sQuery(id+"F7.wireOp",EDGE,"E3.bottom");var subQ4=sQuery(id+"F5.wireOp",EDGE,"E2.left");var subQ5=sQuery(id+"F5.wireOp",EDGE,"E2.top");var subQ6=sQuery(id+"F2.wireOp",EDGE,"E1.right");var subQ7=sQuery(id+"F2.wireOp",EDGE,"E1.bottom");var subQ8=sQuery(id+"F0.wireOp",EDGE,"E0.right");var subQ16=sQuery(id+"F14.wireOp",EDGE,"E5.bottom");var subQ18=sQuery(id+"F14.wireOp",EDGE,"E5.right");Q1=makeQuery(id+"F32.boolean.opBoolean","SPLIT",FACE,{"disambiguationData":[TD([makeQuery(id+"F28.opExtrude","SWEPT_FACE",FACE,{"disambiguationData":[OSD([sQuery(id+"F27.wireOp",EDGE,"E9.right")])]})])],"derivedFrom":makeQuery(id+"F24.boolean.opBoolean","MERGE",FACE,{"derivedFrom":[makeQuery(id+"F20.boolean.opBoolean","MERGE",FACE,{"derivedFrom":[makeQuery(id+"F18.boolean.opBoolean","MERGE",FACE,{"derivedFrom":[makeQuery(id+"F16.boolean.opBoolean","MERGE",FACE,{"derivedFrom":[makeQuery(id+"F15.opExtrude","SWEPT_FACE",FACE,{"disambiguationData":[OSD([subQ18])]}),makeQuery(id+"F16.opExtrude","SWEPT_FACE",FACE,{"disambiguationData":[OSD([subQ8,subQ7,subQ6,subQ5,subQ4,subQ3,subQ2,subQ1,subQ0,subQ16,subQ18])]})]}),makeQuery(id+"F18.opExtrude","SWEPT_FACE",FACE,{"disambiguationData":[OSD([subQ8,subQ7,subQ6,subQ5,subQ4,subQ3,subQ2,subQ1,subQ0,subQ16,subQ18])]})]}),makeQuery(id+"F20.opExtrude","SWEPT_FACE",FACE,{"disambiguationData":[OSD([subQ8,subQ7,subQ6,subQ5,subQ4,subQ3,subQ2,subQ1,subQ0,subQ16,subQ18])]})]}),makeQuery(id+"F24.opExtrude","SWEPT_FACE",FACE,{"disambiguationData":[OSD([subQ8,subQ7,subQ6,subQ5,subQ4,subQ3,subQ2,subQ1,subQ0,subQ16,subQ18])]})]})});}
            extrude(context, id + "F36", {"entities" : qUnion([Q0]), "operationType" : NewBodyOperationType.REMOVE, "endBound" : BoundingType.UP_TO_SURFACE, "oppositeDirection" : true, "endBoundEntityFace" : qUnion([Q1]), "depth" : 25.4 * mm});
        }
        {
            var Q0;
            {var subQ0=sQuery(id+"F14.wireOp",EDGE,"E5.left");var subQ2=sQuery(id+"F12.wireOp",EDGE,"E4.left");var subQ4=sQuery(id+"F5.wireOp",EDGE,"E2.right");var subQ6=sQuery(id+"F2.wireOp",EDGE,"E1.left");var subQ9=sQuery(id+"F12.wireOp",EDGE,"E4.bottom");var subQ10=sQuery(id+"F5.wireOp",EDGE,"E2.top");var subQ11=sQuery(id+"F2.wireOp",EDGE,"E1.bottom");var subQ12=sQuery(id+"F0.wireOp",EDGE,"E0.left");Q0=makeQuery(id+"F34.boolean.opBoolean","SPLIT",FACE,{"disambiguationData":[TD([makeQuery(id+"F15.opExtrude","SWEPT_FACE",FACE,{"disambiguationData":[OSD([subQ0])]})])],"derivedFrom":makeQuery(id+"F23.opExtrude","CAP_FACE",FACE,{"disambiguationData":[OSD([subQ12,subQ11,subQ6,subQ10,subQ4,subQ9,subQ2])],"isStart":false})});}
            var Q1;
            Q1=makeQuery(id+"F32.boolean.opBoolean","MERGE",FACE,{"derivedFrom":[makeQuery(id+"F30.boolean.opBoolean","MERGE",FACE,{"derivedFrom":[makeQuery(id+"F28.opExtrude","SWEPT_FACE",FACE,{"disambiguationData":[OSD([sQuery(id+"F27.wireOp",EDGE,"E9.right")])]}),makeQuery(id+"F30.opExtrude","SWEPT_FACE",FACE,{"disambiguationData":[OSD([sQuery(id+"F29.wireOp",EDGE,"E10.right")])]})]}),makeQuery(id+"F32.opExtrude","SWEPT_FACE",FACE,{"disambiguationData":[OSD([sQuery(id+"F31.wireOp",EDGE,"E11.left")])]})]});
            extrude(context, id + "F37", {"entities" : qUnion([Q0]), "operationType" : NewBodyOperationType.REMOVE, "endBound" : BoundingType.UP_TO_SURFACE, "oppositeDirection" : true, "endBoundEntityFace" : qUnion([Q1]), "depth" : 25.4 * mm});
        }
        {
            var Q0;
            {var subQ0=sQuery(id+"F0.wireOp",EDGE,"E0.bottom");Q0=makeQuery(id+"F23.boolean.opBoolean","MERGE",FACE,{"derivedFrom":[makeQuery(id+"F1.opExtrude","SWEPT_FACE",FACE,{"disambiguationData":[OSD([subQ0])]}),makeQuery(id+"F23.opExtrude","SWEPT_FACE",FACE,{"disambiguationData":[OSD([subQ0,sQuery(id+"F0.wireOp",EDGE,"E0.left")])]})]});}
            extrude(context, id + "F38", {"entities" : qUnion([Q0]), "operationType" : NewBodyOperationType.ADD, "depth" : 76.2 * mm});
        }
        {
            var Q0;
            {var subQ0=sQuery(id+"F0.wireOp",EDGE,"E0.top");Q0=makeQuery(id+"F23.boolean.opBoolean","MERGE",FACE,{"derivedFrom":[makeQuery(id+"F1.opExtrude","SWEPT_FACE",FACE,{"disambiguationData":[OSD([subQ0])]}),makeQuery(id+"F23.opExtrude","SWEPT_FACE",FACE,{"disambiguationData":[OSD([subQ0,sQuery(id+"F0.wireOp",EDGE,"E0.left")])]})]});}
            extrude(context, id + "F39", {"entities" : qUnion([Q0]), "operationType" : NewBodyOperationType.REMOVE, "oppositeDirection" : true, "depth" : 76.2 * mm});
        }
        {
            var Q0;
            {var subQ0=sQuery(id+"F12.wireOp",EDGE,"E4.left");var subQ1=sQuery(id+"F12.wireOp",EDGE,"E4.bottom");var subQ2=sQuery(id+"F14.wireOp",EDGE,"E5.left");var subQ3=sQuery(id+"F14.wireOp",EDGE,"E5.bottom");Q0=makeQuery(id+"F23.boolean.opBoolean","MERGE",FACE,{"derivedFrom":[makeQuery(id+"F20.boolean.opBoolean","MERGE",FACE,{"derivedFrom":[makeQuery(id+"F18.boolean.opBoolean","MERGE",FACE,{"derivedFrom":[makeQuery(id+"F16.boolean.opBoolean","MERGE",FACE,{"derivedFrom":[makeQuery(id+"F15.boolean.opBoolean","MERGE",FACE,{"derivedFrom":[makeQuery(id+"F13.opExtrude","CAP_FACE",FACE,{"disambiguationData":[OSD([subQ1,sQuery(id+"F12.wireOp",EDGE,"E4.top"),subQ0,sQuery(id+"F12.wireOp",EDGE,"E4.right")])],"isStart":false}),makeQuery(id+"F15.opExtrude","SWEPT_FACE",FACE,{"disambiguationData":[OSD([subQ2])]})]}),makeQuery(id+"F16.opExtrude","SWEPT_FACE",FACE,{"disambiguationData":[OSD([subQ1,subQ3,subQ2])]})]}),makeQuery(id+"F18.opExtrude","SWEPT_FACE",FACE,{"disambiguationData":[OSD([subQ1,subQ3,subQ2])]})]}),makeQuery(id+"F20.opExtrude","SWEPT_FACE",FACE,{"disambiguationData":[OSD([subQ3,subQ2])]})]}),makeQuery(id+"F23.opExtrude","SWEPT_FACE",FACE,{"disambiguationData":[OSD([subQ1,subQ0])]})]});}
            extrude(context, id + "F40", {"entities" : qUnion([Q0]), "operationType" : NewBodyOperationType.ADD, "depth" : 50.8 * mm});
        }
        {
            var Q0;
            {var subQ6=sQuery(id+"F12.wireOp",EDGE,"E4.bottom");var subQ7=sQuery(id+"F5.wireOp",EDGE,"E2.top");var subQ8=sQuery(id+"F2.wireOp",EDGE,"E1.bottom");var subQ10=sQuery(id+"F14.wireOp",EDGE,"E5.bottom");var subQ11=sQuery(id+"F7.wireOp",EDGE,"E3.right");var subQ12=sQuery(id+"F7.wireOp",EDGE,"E3.bottom");var subQ13=sQuery(id+"F5.wireOp",EDGE,"E2.left");var subQ14=sQuery(id+"F14.wireOp",EDGE,"E5.right");var subQ16=sQuery(id+"F12.wireOp",EDGE,"E4.right");var subQ17=sQuery(id+"F2.wireOp",EDGE,"E1.right");var subQ18=sQuery(id+"F0.wireOp",EDGE,"E0.right");Q0=makeQuery(id+"F32.boolean.opBoolean","SPLIT",FACE,{"disambiguationData":[TD([makeQuery(id+"F22.opExtrude","SWEPT_FACE",FACE,{"disambiguationData":[OSD([sQuery(id+"F21.wireOp",EDGE,"E6.left")])]})])],"derivedFrom":makeQuery(id+"F24.boolean.opBoolean","MERGE",FACE,{"derivedFrom":[makeQuery(id+"F20.boolean.opBoolean","MERGE",FACE,{"derivedFrom":[makeQuery(id+"F18.boolean.opBoolean","MERGE",FACE,{"derivedFrom":[makeQuery(id+"F16.boolean.opBoolean","MERGE",FACE,{"derivedFrom":[makeQuery(id+"F15.opExtrude","SWEPT_FACE",FACE,{"disambiguationData":[OSD([subQ14])]}),makeQuery(id+"F16.opExtrude","SWEPT_FACE",FACE,{"disambiguationData":[OSD([subQ18,subQ8,subQ17,subQ7,subQ13,subQ12,subQ11,subQ6,subQ16,subQ10,subQ14])]})]}),makeQuery(id+"F18.opExtrude","SWEPT_FACE",FACE,{"disambiguationData":[OSD([subQ18,subQ8,subQ17,subQ7,subQ13,subQ12,subQ11,subQ6,subQ16,subQ10,subQ14])]})]}),makeQuery(id+"F20.opExtrude","SWEPT_FACE",FACE,{"disambiguationData":[OSD([subQ18,subQ8,subQ17,subQ7,subQ13,subQ12,subQ11,subQ6,subQ16,subQ10,subQ14])]})]}),makeQuery(id+"F24.opExtrude","SWEPT_FACE",FACE,{"disambiguationData":[OSD([subQ18,subQ8,subQ17,subQ7,subQ13,subQ12,subQ11,subQ6,subQ16,subQ10,subQ14])]})]})});}
            extrude(context, id + "F41", {"entities" : qUnion([Q0]), "operationType" : NewBodyOperationType.REMOVE, "oppositeDirection" : true, "depth" : 50.8 * mm});
        }
    });
